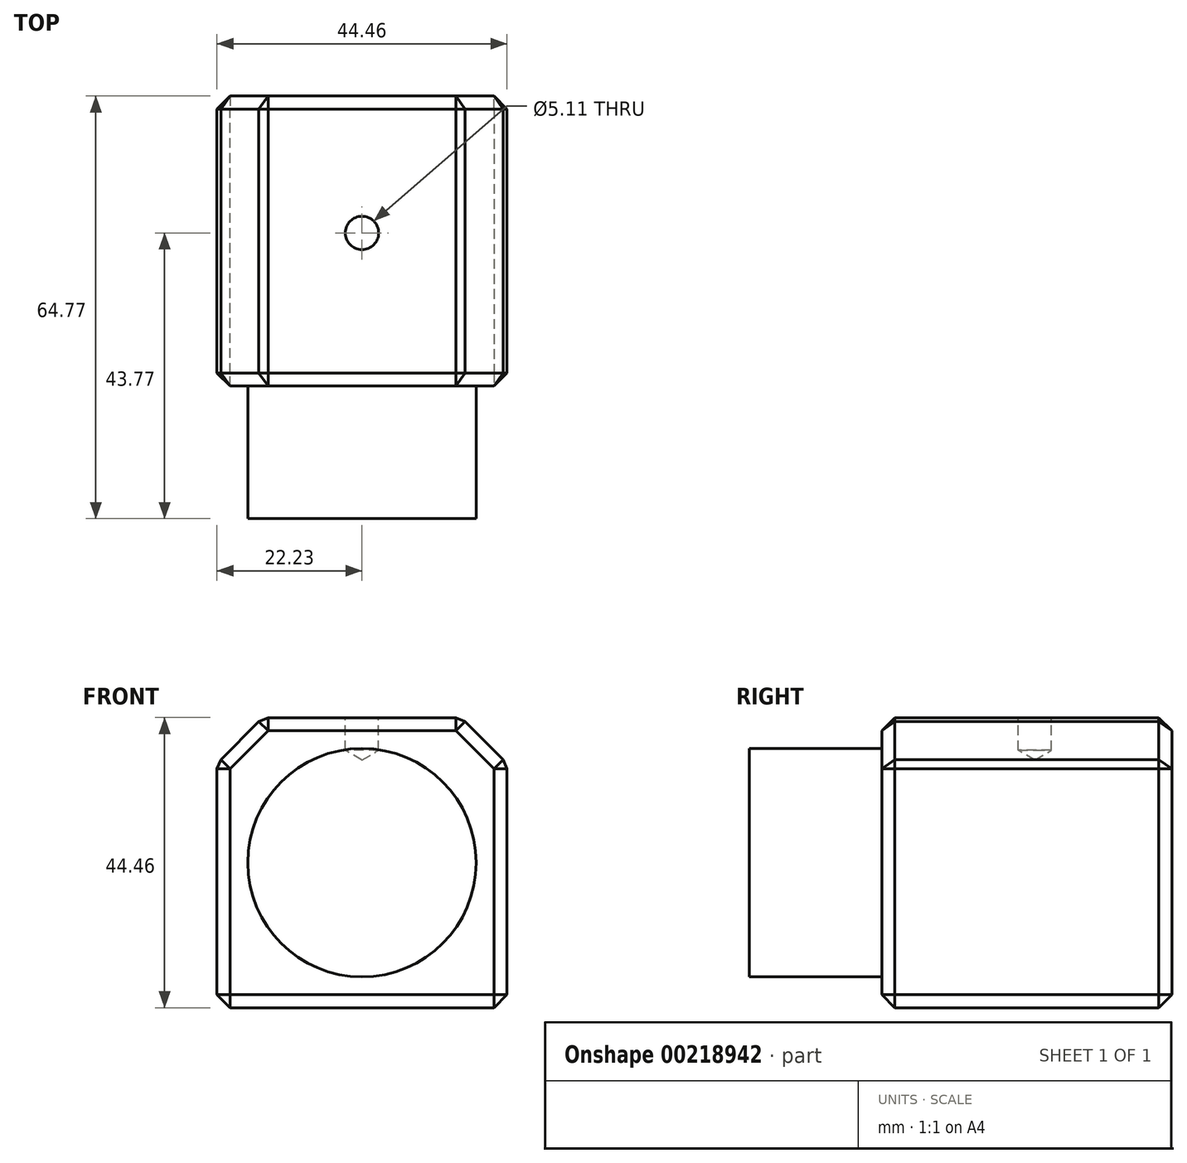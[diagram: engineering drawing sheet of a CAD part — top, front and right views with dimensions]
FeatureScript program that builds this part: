
annotation { "Feature Type Name" : "Feature", "Feature Type Description" : "" }
export const myFeature = defineFeature(function(context is Context, id is Id, definition is map)
    precondition{}
    {
        {
            var Q0;
            Q0=qCreatedBy(makeId("Front.planeOp"),FACE);
            var sketch = newSketch(context, id + "F0", { "sketchPlane" : qUnion([Q0])});
            skLineSegment(sketch, "E0.bottom", {"start": v(22.23, -22.22) * mm, "end": v(-22.22, -22.22) * mm});
            skLineSegment(sketch, "E0.top", {"start": v(22.22, 22.23) * mm, "end": v(-22.23, 22.23) * mm});
            skLineSegment(sketch, "E0.left", {"start": v(22.23, -22.22) * mm, "end": v(22.22, 22.23) * mm});
            skLineSegment(sketch, "E0.right", {"start": v(-22.22, -22.22) * mm, "end": v(-22.23, 22.23) * mm});
            skPoint(sketch, "E0.middle", {"position": v(0, 0) * mm});
            skSolve(sketch);
        }
        {
            var Q0;
            Q0=makeQuery(id+"F0.imprint","IMPRINT",FACE,{"disambiguationData":[TD([[makeQuery(id+"F0.imprint","IMPRINT",EDGE,{"derivedFrom":sQuery(id+"F0.wireOp",EDGE,"E0.bottom")}),-1.0]])]});
            extrude(context, id + "F1", {"entities" : qUnion([Q0]), "depth" : 44.45 * mm});
        }
        {
            var Q0;
            Q0=makeQuery(id+"F1.opExtrude","CAP_FACE",FACE,{"disambiguationData":[OSD([sQuery(id+"F0.wireOp",EDGE,"E0.bottom"),sQuery(id+"F0.wireOp",EDGE,"E0.top"),sQuery(id+"F0.wireOp",EDGE,"E0.left"),sQuery(id+"F0.wireOp",EDGE,"E0.right")])],"isStart":false});
            var sketch = newSketch(context, id + "F2", { "sketchPlane" : qUnion([Q0])});
            skCircle(sketch, "E1", {"center": v(0, 0) * mm, "radius": 17.5 * mm});
            skSolve(sketch);
        }
        {
            var Q0;
            Q0=makeQuery(id+"F2.imprint","IMPRINT",FACE,{"disambiguationData":[TD([[makeQuery(id+"F2.imprint","IMPRINT",EDGE,{"derivedFrom":sQuery(id+"F2.wireOp",EDGE,"E1")}),1.0]])]});
            extrude(context, id + "F3", {"entities" : qUnion([Q0]), "operationType" : NewBodyOperationType.ADD, "depth" : 20.32 * mm});
        }
        {
            var Q0;
            Q0=makeQuery(id+"F1.opExtrude","SWEPT_EDGE",EDGE,{"disambiguationData":[OSD([sQuery(id+"F0.wireOp",EDGE,"E0.top"),sQuery(id+"F0.wireOp",EDGE,"E0.right")])]});
            var Q1;
            Q1=makeQuery(id+"F1.opExtrude","SWEPT_EDGE",EDGE,{"disambiguationData":[OSD([sQuery(id+"F0.wireOp",EDGE,"E0.top"),sQuery(id+"F0.wireOp",EDGE,"E0.left")])]});
            chamfer(context, id + "F4", {"entities" : qUnion([Q0, Q1]), "width" : 7 * mm, "tangentPropagation" : true});
        }
        {
            var Q0;
            Q0=makeQuery(id+"F1.opExtrude","CAP_EDGE",EDGE,{"disambiguationData":[OSD([sQuery(id+"F0.wireOp",EDGE,"E0.top")])],"isStart":false});
            var Q1;
            {var subQ0=sQuery(id+"F0.wireOp",EDGE,"E0.right");var subQ1=sQuery(id+"F0.wireOp",EDGE,"E0.top");Q1=makeQuery(id+"F4.opChamfer","BLEND_EDGE",EDGE,{"blendedFrom":[makeQuery(id+"F1.opExtrude","SWEPT_EDGE",EDGE,{"disambiguationData":[OSD([subQ1,subQ0])]}),makeQuery(id+"F1.opExtrude","CAP_FACE",FACE,{"disambiguationData":[OSD([sQuery(id+"F0.wireOp",EDGE,"E0.bottom"),subQ1,sQuery(id+"F0.wireOp",EDGE,"E0.left"),subQ0])],"isStart":false})],"blendedInto":[makeQuery(id+"F1.opExtrude","CAP_FACE",FACE,{"disambiguationData":[OSD([sQuery(id+"F0.wireOp",EDGE,"E0.bottom"),subQ1,sQuery(id+"F0.wireOp",EDGE,"E0.left"),subQ0])],"isStart":false})]});}
            var Q2;
            Q2=makeQuery(id+"F1.opExtrude","CAP_EDGE",EDGE,{"disambiguationData":[OSD([sQuery(id+"F0.wireOp",EDGE,"E0.right")])],"isStart":false});
            var Q3;
            Q3=makeQuery(id+"F1.opExtrude","SWEPT_EDGE",EDGE,{"disambiguationData":[OSD([sQuery(id+"F0.wireOp",EDGE,"E0.bottom"),sQuery(id+"F0.wireOp",EDGE,"E0.right")])]});
            var Q4;
            {var subQ0=sQuery(id+"F0.wireOp",EDGE,"E0.left");var subQ1=sQuery(id+"F0.wireOp",EDGE,"E0.top");Q4=makeQuery(id+"F4.opChamfer","BLEND_EDGE",EDGE,{"blendedFrom":[makeQuery(id+"F1.opExtrude","SWEPT_EDGE",EDGE,{"disambiguationData":[OSD([subQ1,subQ0])]}),makeQuery(id+"F1.opExtrude","CAP_FACE",FACE,{"disambiguationData":[OSD([sQuery(id+"F0.wireOp",EDGE,"E0.bottom"),subQ1,subQ0,sQuery(id+"F0.wireOp",EDGE,"E0.right")])],"isStart":false})],"blendedInto":[makeQuery(id+"F1.opExtrude","CAP_FACE",FACE,{"disambiguationData":[OSD([sQuery(id+"F0.wireOp",EDGE,"E0.bottom"),subQ1,subQ0,sQuery(id+"F0.wireOp",EDGE,"E0.right")])],"isStart":false})]});}
            var Q5;
            Q5=makeQuery(id+"F1.opExtrude","CAP_EDGE",EDGE,{"disambiguationData":[OSD([sQuery(id+"F0.wireOp",EDGE,"E0.left")])],"isStart":false});
            var Q6;
            Q6=makeQuery(id+"F1.opExtrude","CAP_EDGE",EDGE,{"disambiguationData":[OSD([sQuery(id+"F0.wireOp",EDGE,"E0.bottom")])],"isStart":false});
            var Q7;
            Q7=makeQuery(id+"F1.opExtrude","SWEPT_EDGE",EDGE,{"disambiguationData":[OSD([sQuery(id+"F0.wireOp",EDGE,"E0.bottom"),sQuery(id+"F0.wireOp",EDGE,"E0.left")])]});
            var Q8;
            {var subQ0=sQuery(id+"F0.wireOp",EDGE,"E0.right");Q8=makeQuery(id+"F4.opChamfer","BLEND_EDGE",EDGE,{"blendedFrom":[makeQuery(id+"F1.opExtrude","SWEPT_EDGE",EDGE,{"disambiguationData":[OSD([sQuery(id+"F0.wireOp",EDGE,"E0.top"),subQ0])]}),makeQuery(id+"F1.opExtrude","SWEPT_FACE",FACE,{"disambiguationData":[OSD([subQ0])]})],"blendedInto":[makeQuery(id+"F1.opExtrude","SWEPT_FACE",FACE,{"disambiguationData":[OSD([subQ0])]})]});}
            var Q9;
            {var subQ0=sQuery(id+"F0.wireOp",EDGE,"E0.top");Q9=makeQuery(id+"F4.opChamfer","BLEND_EDGE",EDGE,{"blendedFrom":[makeQuery(id+"F1.opExtrude","SWEPT_EDGE",EDGE,{"disambiguationData":[OSD([subQ0,sQuery(id+"F0.wireOp",EDGE,"E0.right")])]}),makeQuery(id+"F1.opExtrude","SWEPT_FACE",FACE,{"disambiguationData":[OSD([subQ0])]})],"blendedInto":[makeQuery(id+"F1.opExtrude","SWEPT_FACE",FACE,{"disambiguationData":[OSD([subQ0])]})]});}
            var Q10;
            {var subQ0=sQuery(id+"F0.wireOp",EDGE,"E0.left");Q10=makeQuery(id+"F4.opChamfer","BLEND_EDGE",EDGE,{"blendedFrom":[makeQuery(id+"F1.opExtrude","SWEPT_EDGE",EDGE,{"disambiguationData":[OSD([sQuery(id+"F0.wireOp",EDGE,"E0.top"),subQ0])]}),makeQuery(id+"F1.opExtrude","SWEPT_FACE",FACE,{"disambiguationData":[OSD([subQ0])]})],"blendedInto":[makeQuery(id+"F1.opExtrude","SWEPT_FACE",FACE,{"disambiguationData":[OSD([subQ0])]})]});}
            var Q11;
            {var subQ0=sQuery(id+"F0.wireOp",EDGE,"E0.top");Q11=makeQuery(id+"F4.opChamfer","BLEND_EDGE",EDGE,{"blendedFrom":[makeQuery(id+"F1.opExtrude","SWEPT_EDGE",EDGE,{"disambiguationData":[OSD([subQ0,sQuery(id+"F0.wireOp",EDGE,"E0.left")])]}),makeQuery(id+"F1.opExtrude","SWEPT_FACE",FACE,{"disambiguationData":[OSD([subQ0])]})],"blendedInto":[makeQuery(id+"F1.opExtrude","SWEPT_FACE",FACE,{"disambiguationData":[OSD([subQ0])]})]});}
            var Q12;
            Q12=makeQuery(id+"F1.opExtrude","CAP_FACE",FACE,{"disambiguationData":[OSD([sQuery(id+"F0.wireOp",EDGE,"E0.bottom"),sQuery(id+"F0.wireOp",EDGE,"E0.top"),sQuery(id+"F0.wireOp",EDGE,"E0.left"),sQuery(id+"F0.wireOp",EDGE,"E0.right")])],"isStart":true});
            chamfer(context, id + "F5", {"entities" : qUnion([Q0, Q1, Q2, Q3, Q4, Q5, Q6, Q7, Q8, Q9, Q10, Q11, Q12]), "width" : 2 * mm, "tangentPropagation" : true});
        }
        {
            var Q0;
            Q0=makeQuery(id+"F1.opExtrude","SWEPT_FACE",FACE,{"disambiguationData":[OSD([sQuery(id+"F0.wireOp",EDGE,"E0.top")])]});
            var sketch = newSketch(context, id + "F6", { "sketchPlane" : qUnion([Q0])});
            skLineSegment(sketch, "E2.0.0", {"start": v(-20.23, 0) * mm, "end": v(-14.4, 0) * mm, "construction": true});
            skLineSegment(sketch, "E2.0.1", {"start": v(-14.4, 0) * mm, "end": v(14.4, 0) * mm, "construction": true});
            skLineSegment(sketch, "E2.0.2", {"start": v(14.4, 0) * mm, "end": v(20.22, 0) * mm, "construction": true});
            skLineSegment(sketch, "E2.0.4", {"start": v(20.23, 0) * mm, "end": v(-20.22, 0) * mm, "construction": true});
            skPoint(sketch, "E3", {"position": v(0, -21) * mm});
            skPoint(sketch, "E3.positionSnap0", {"position": v(0, -2) * mm});
            skSolve(sketch);
        }
        {
            var Q0;
            Q0=sQuery(id+"F6.wireOp",VERTEX,"E3");
            var Q1;
            Q1=makeQuery(id+"F1.opExtrude","SWEPT_BODY",BODY,{"disambiguationData":[OSD([sQuery(id+"F0.wireOp",EDGE,"E0.bottom"),sQuery(id+"F0.wireOp",EDGE,"E0.top"),sQuery(id+"F0.wireOp",EDGE,"E0.left"),sQuery(id+"F0.wireOp",EDGE,"E0.right")])]});
            hole(context, id + "F7", {"style" : HoleStyle.SIMPLE, "endStyle" : HoleEndStyle.BLIND, "standardTappedOrClearance" : lookupTablePath({ "standard" : "ANSI", "engagement" : "75%", "pitch" : "20 tpi", "size" : "1/4", "type" : "Tapped" }), "standardBlindInLast" : lookupTablePath({ "standard" : "ANSI", "engagement" : "75%", "pitch" : "20 tpi", "size" : "1/4", "type" : "Tapped" }), "holeDiameter" : 5.1 * mm, "holeDepth" : 5 * mm, "locations" : qUnion([Q0]), "scope" : qUnion([Q1]), "majorDiameter" : 6.35 * mm});
        }
    });
